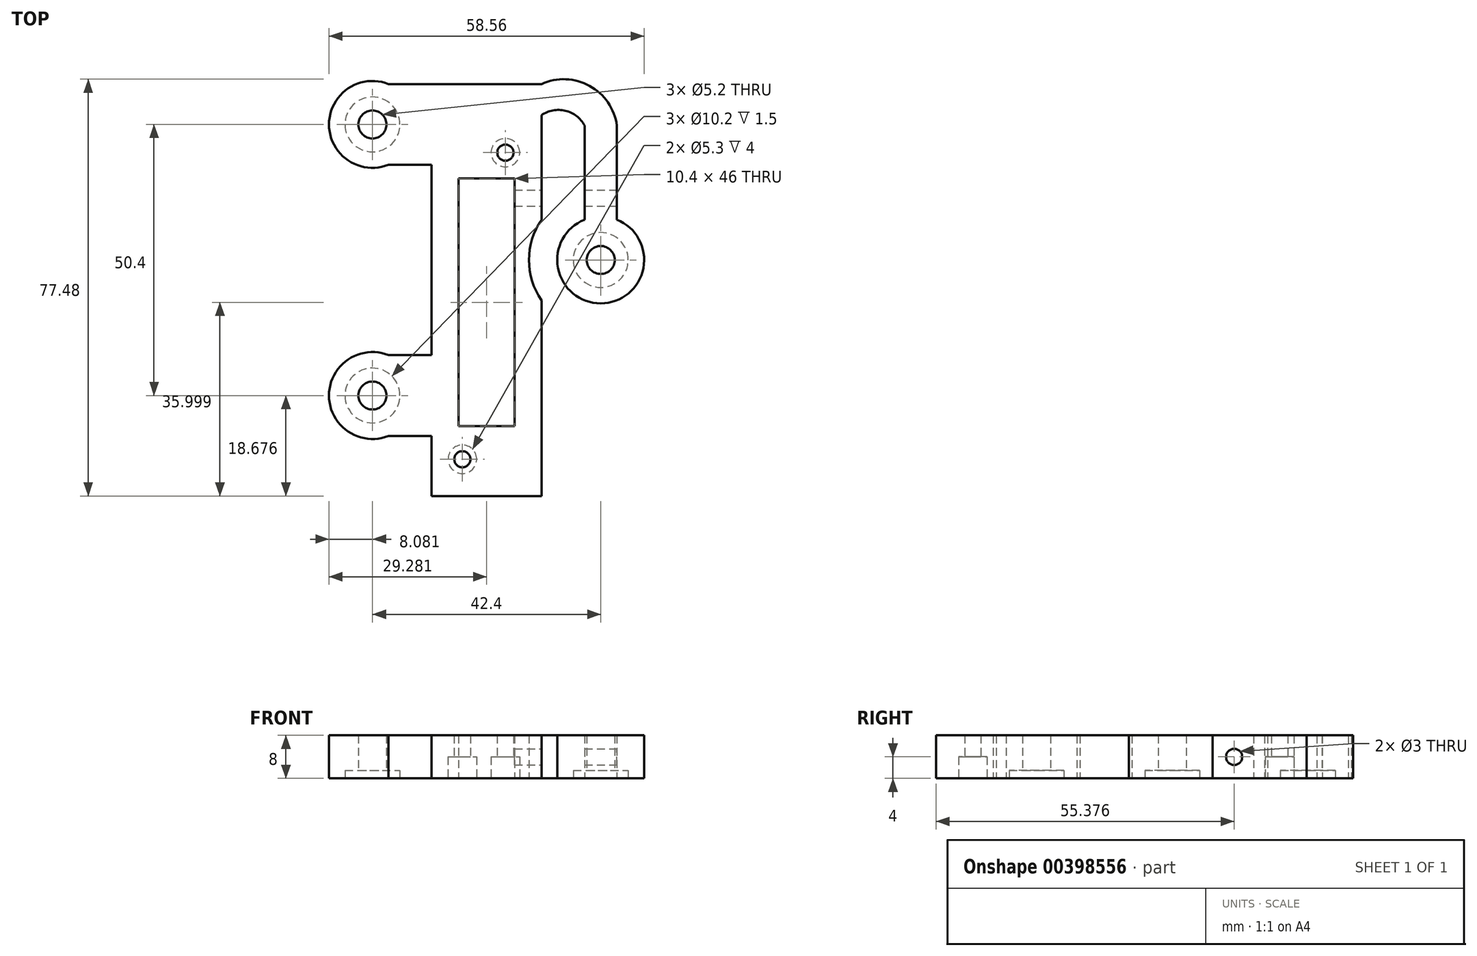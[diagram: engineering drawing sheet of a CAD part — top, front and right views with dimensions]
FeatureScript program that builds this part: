
annotation { "Feature Type Name" : "Feature", "Feature Type Description" : "" }
export const myFeature = defineFeature(function(context is Context, id is Id, definition is map)
    precondition{}
    {
        {
            var Q0;
            Q0=qCreatedBy(makeId("Top.planeOp"),FACE);
            var sketch = newSketch(context, id + "F0", { "sketchPlane" : qUnion([Q0])});
            skPoint(sketch, "E0", {"position": v(-7.75, -32.46) * mm});
            skPoint(sketch, "E1", {"position": v(0.25, 24.54) * mm});
            skCircle(sketch, "E2", {"center": v(0.25, 24.54) * mm, "radius": 1.5 * mm});
            skCircle(sketch, "E3", {"center": v(-7.75, -32.46) * mm, "radius": 1.5 * mm});
            skLineSegment(sketch, "E4.1", {"start": v(6.95, 37.29) * mm, "end": v(-13.45, 37.29) * mm});
            skLineSegment(sketch, "E4.2", {"start": v(6.95, -28.11) * mm, "end": v(6.95, 37.29) * mm});
            skLineSegment(sketch, "E4.3", {"start": v(-13.45, -28.11) * mm, "end": v(-13.45, 37.29) * mm});
            skLineSegment(sketch, "E5.bottom", {"start": v(-13.45, 37.29) * mm, "end": v(-21.45, 37.29) * mm});
            skLineSegment(sketch, "E5.top", {"start": v(-13.45, 22.29) * mm, "end": v(-21.45, 22.29) * mm});
            skLineSegment(sketch, "E5.left", {"start": v(-13.45, 37.29) * mm, "end": v(-13.45, 22.29) * mm});
            skLineSegment(sketch, "E5.right", {"start": v(-21.45, 37.29) * mm, "end": v(-21.45, 22.29) * mm});
            skLineSegment(sketch, "E6.bottom", {"start": v(-13.45, -28.11) * mm, "end": v(-21.45, -28.11) * mm});
            skLineSegment(sketch, "E6.top", {"start": v(-13.45, -13.11) * mm, "end": v(-21.45, -13.11) * mm});
            skLineSegment(sketch, "E6.left", {"start": v(-13.45, -28.11) * mm, "end": v(-13.45, -13.11) * mm});
            skLineSegment(sketch, "E6.right", {"start": v(-21.45, -28.11) * mm, "end": v(-21.45, -13.11) * mm});
            skLineSegment(sketch, "E7.left", {"start": v(6.95, 12.09) * mm, "end": v(6.95, -2.91) * mm});
            skLineSegment(sketch, "E7.right", {"start": v(14.95, 12.09) * mm, "end": v(14.95, -2.91) * mm});
            skPoint(sketch, "E8", {"position": v(17.95, 4.59) * mm});
            skPoint(sketch, "E8.positionSnap0", {"position": v(14.95, 4.59) * mm});
            skPoint(sketch, "E9", {"position": v(-24.45, -20.61) * mm});
            skPoint(sketch, "E9.positionSnap0", {"position": v(-21.45, -20.61) * mm});
            skPoint(sketch, "E10", {"position": v(-24.45, 29.79) * mm});
            skPoint(sketch, "E10.positionSnap0", {"position": v(-21.45, 29.79) * mm});
            skCircle(sketch, "E11", {"center": v(-24.45, 29.79) * mm, "radius": 8.08 * mm});
            skCircle(sketch, "E12", {"center": v(17.95, 4.59) * mm, "radius": 8.08 * mm});
            skCircle(sketch, "E13", {"center": v(-24.45, -20.61) * mm, "radius": 8.08 * mm});
            skArc(sketch, "E14", {"start": v(6.95, 12.09) * mm, "mid": v(4.64, 4.59) * mm, "end": v(6.95, -2.91) * mm});
            skLineSegment(sketch, "E15.bottom", {"start": v(14.95, 12.09) * mm, "end": v(20.95, 12.09) * mm});
            skLineSegment(sketch, "E15.left", {"start": v(14.95, 12.09) * mm, "end": v(14.95, 29.58) * mm});
            skLineSegment(sketch, "E15.right", {"start": v(20.95, 12.09) * mm, "end": v(20.95, 29.58) * mm});
            skPoint(sketch, "E16.third.point", {"position": v(11.8, 18.33) * mm});
            skArc(sketch, "E17", {"start": v(14.95, 29.58) * mm, "mid": v(11.38, 32.33) * mm, "end": v(6.95, 31.48) * mm});
            skPoint(sketch, "E17.second.point", {"position": v(6.95, 31.48) * mm});
            skPoint(sketch, "E17.third.point", {"position": v(4.8, 25.59) * mm});
            skArc(sketch, "E18.trimOffspring", {"start": v(20.95, 26.92) * mm, "mid": v(17.02, 36.24) * mm, "end": v(6.95, 37.29) * mm});
            skLineSegment(sketch, "E19.bottom", {"start": v(1.2, 19.7) * mm, "end": v(-1.2, 19.7) * mm});
            skPoint(sketch, "E20", {"position": v(6.95, 16.9) * mm});
            skPoint(sketch, "E20.positionSnap0", {"position": v(1.2, 16.9) * mm});
            skLineSegment(sketch, "E21", {"start": v(-13.45, -28.11) * mm, "end": v(-13.45, -39.3) * mm});
            skLineSegment(sketch, "E22", {"start": v(-13.45, -39.3) * mm, "end": v(6.95, -39.3) * mm});
            skLineSegment(sketch, "E23", {"start": v(6.95, -39.3) * mm, "end": v(6.95, -28.11) * mm});
            skPoint(sketch, "E4.0.start.orphan", {"position": v(6.95, -28.11) * mm});
            skLineSegment(sketch, "E24.bottom", {"start": v(1.95, -26.3) * mm, "end": v(-8.45, -26.3) * mm});
            skLineSegment(sketch, "E24.top", {"start": v(1.95, 19.7) * mm, "end": v(-8.45, 19.7) * mm});
            skLineSegment(sketch, "E24.left", {"start": v(1.95, -26.3) * mm, "end": v(1.95, 19.7) * mm});
            skLineSegment(sketch, "E24.right", {"start": v(-8.45, -26.3) * mm, "end": v(-8.45, 19.7) * mm});
            skSolve(sketch);
        }
        {
            var Q0;
            {var subQ0=sQuery(id+"F0.wireOp",EDGE,"E5.right");Q0=makeQuery(id+"F0.imprint","IMPRINT",FACE,{"disambiguationData":[TD([[makeQuery(id+"F0.imprint","IMPRINT",EDGE,{"derivedFrom":subQ0}),-1.0]])]});}
            var Q1;
            {var subQ0=sQuery(id+"F0.wireOp",EDGE,"E5.right");Q1=makeQuery(id+"F0.imprint","IMPRINT",FACE,{"disambiguationData":[TD([[makeQuery(id+"F0.imprint","IMPRINT",EDGE,{"derivedFrom":subQ0}),1.0]])]});}
            var Q2;
            {var subQ0=sQuery(id+"F0.wireOp",EDGE,"E5.bottom");Q2=makeQuery(id+"F0.imprint","IMPRINT",FACE,{"disambiguationData":[TD([[makeQuery(id+"F0.imprint","IMPRINT",EDGE,{"derivedFrom":subQ0}),1.0]])]});}
            var Q3;
            Q3=makeQuery(id+"F0.imprint","IMPRINT",FACE,{"disambiguationData":[TD([[makeQuery(id+"F0.imprint","IMPRINT",EDGE,{"derivedFrom":sQuery(id+"F0.wireOp",EDGE,"E2")}),-1.0]])]});
            var Q4;
            {var subQ9=sQuery(id+"F0.wireOp",EDGE,"E15.left");Q4=makeQuery(id+"F0.imprint","IMPRINT",FACE,{"disambiguationData":[TD([[makeQuery(id+"F0.imprint","IMPRINT",EDGE,{"derivedFrom":subQ9}),-1.0]])]});}
            var Q5;
            {var subQ0=sQuery(id+"F0.wireOp",EDGE,"E7.right");Q5=makeQuery(id+"F0.imprint","IMPRINT",FACE,{"disambiguationData":[TD([[makeQuery(id+"F0.imprint","IMPRINT",EDGE,{"derivedFrom":subQ0}),1.0]])]});}
            var Q6;
            {var subQ0=sQuery(id+"F0.wireOp",EDGE,"E15.bottom");Q6=makeQuery(id+"F0.imprint","IMPRINT",FACE,{"disambiguationData":[TD([[makeQuery(id+"F0.imprint","IMPRINT",EDGE,{"derivedFrom":subQ0}),1.0]])]});}
            var Q7;
            {var subQ0=sQuery(id+"F0.wireOp",EDGE,"E7.right");Q7=makeQuery(id+"F0.imprint","IMPRINT",FACE,{"disambiguationData":[TD([[makeQuery(id+"F0.imprint","IMPRINT",EDGE,{"derivedFrom":subQ0}),-1.0]])]});}
            var Q8;
            {var subQ0=sQuery(id+"F0.wireOp",EDGE,"E6.bottom");Q8=makeQuery(id+"F0.imprint","IMPRINT",FACE,{"disambiguationData":[TD([[makeQuery(id+"F0.imprint","IMPRINT",EDGE,{"derivedFrom":subQ0}),-1.0]])]});}
            var Q9;
            {var subQ0=sQuery(id+"F0.wireOp",EDGE,"E6.right");Q9=makeQuery(id+"F0.imprint","IMPRINT",FACE,{"disambiguationData":[TD([[makeQuery(id+"F0.imprint","IMPRINT",EDGE,{"derivedFrom":subQ0}),-1.0]])]});}
            var Q10;
            {var subQ0=sQuery(id+"F0.wireOp",EDGE,"E6.right");Q10=makeQuery(id+"F0.imprint","IMPRINT",FACE,{"disambiguationData":[TD([[makeQuery(id+"F0.imprint","IMPRINT",EDGE,{"derivedFrom":subQ0}),1.0]])]});}
            extrude(context, id + "F1", {"entities" : qUnion([Q0, Q1, Q2, Q3, Q4, Q5, Q6, Q7, Q8, Q9, Q10]), "depth" : 8 * mm, "offsetDistance" : 25 * mm});
        }
        {
            var Q0;
            Q0=sQuery(id+"F0.wireOp",VERTEX,"E8");
            var Q1;
            Q1=sQuery(id+"F0.wireOp",VERTEX,"E10");
            var Q2;
            Q2=sQuery(id+"F0.wireOp",VERTEX,"E9");
            var Q3;
            Q3=makeQuery(id+"F1.opExtrude","SWEPT_BODY",BODY,{"disambiguationData":[OSD([sQuery(id+"F0.wireOp",EDGE,"E2"),sQuery(id+"F0.wireOp",EDGE,"E3"),sQuery(id+"F0.wireOp",EDGE,"E4.0"),sQuery(id+"F0.wireOp",EDGE,"E4.1"),sQuery(id+"F0.wireOp",EDGE,"E4.2"),sQuery(id+"F0.wireOp",EDGE,"E4.3"),sQuery(id+"F0.wireOp",EDGE,"E5.bottom"),sQuery(id+"F0.wireOp",EDGE,"E5.top"),sQuery(id+"F0.wireOp",EDGE,"E6.bottom"),sQuery(id+"F0.wireOp",EDGE,"E6.top"),sQuery(id+"F0.wireOp",EDGE,"E11"),sQuery(id+"F0.wireOp",EDGE,"E12"),sQuery(id+"F0.wireOp",EDGE,"E13"),sQuery(id+"F0.wireOp",EDGE,"E14"),sQuery(id+"F0.wireOp",EDGE,"E15.left"),sQuery(id+"F0.wireOp",EDGE,"E15.right"),sQuery(id+"F0.wireOp",EDGE,"E17"),sQuery(id+"F0.wireOp",EDGE,"E18.trimOffspring"),sQuery(id+"F0.wireOp",EDGE,"E19.bottom"),sQuery(id+"F0.wireOp",EDGE,"E19.top"),sQuery(id+"F0.wireOp",EDGE,"E19.left"),sQuery(id+"F0.wireOp",EDGE,"E19.right")])]});
            hole(context, id + "F2", {"style" : HoleStyle.C_BORE, "endStyle" : HoleEndStyle.BLIND, "oppositeDirection" : true, "holeDiameter" : 5.2 * mm, "cBoreDiameter" : 10.2 * mm, "cBoreDepth" : 1.5 * mm, "majorDiameter" : 5 * mm, "holeDepth" : 30 * mm, "isTappedThrough" : true, "tappedDepth" : 12 * mm, "tapClearance" : 3, "locations" : qUnion([Q0, Q1, Q2]), "scope" : qUnion([Q3])});
        }
        {
            var Q0;
            Q0=makeQuery(id+"F1.opExtrude","SWEPT_FACE",FACE,{"disambiguationData":[OSD([sQuery(id+"F0.wireOp",EDGE,"E15.right")])]});
            var sketch = newSketch(context, id + "F3", { "sketchPlane" : qUnion([Q0])});
            skPoint(sketch, "E25", {"position": v(16.09, 4) * mm});
            skSolve(sketch);
        }
        {
            var Q0;
            Q0=sQuery(id+"F3.wireOp",VERTEX,"E25");
            var Q1;
            Q1=makeQuery(id+"F1.opExtrude","SWEPT_BODY",BODY,{"disambiguationData":[OSD([sQuery(id+"F0.wireOp",EDGE,"E2"),sQuery(id+"F0.wireOp",EDGE,"E3"),sQuery(id+"F0.wireOp",EDGE,"E4.1"),sQuery(id+"F0.wireOp",EDGE,"E4.2"),sQuery(id+"F0.wireOp",EDGE,"E4.3"),sQuery(id+"F0.wireOp",EDGE,"E5.bottom"),sQuery(id+"F0.wireOp",EDGE,"E5.top"),sQuery(id+"F0.wireOp",EDGE,"E6.bottom"),sQuery(id+"F0.wireOp",EDGE,"E6.top"),sQuery(id+"F0.wireOp",EDGE,"E11"),sQuery(id+"F0.wireOp",EDGE,"E12"),sQuery(id+"F0.wireOp",EDGE,"E13"),sQuery(id+"F0.wireOp",EDGE,"E14"),sQuery(id+"F0.wireOp",EDGE,"E15.left"),sQuery(id+"F0.wireOp",EDGE,"E15.right"),sQuery(id+"F0.wireOp",EDGE,"E17"),sQuery(id+"F0.wireOp",EDGE,"E18.trimOffspring"),sQuery(id+"F0.wireOp",EDGE,"E21"),sQuery(id+"F0.wireOp",EDGE,"E22"),sQuery(id+"F0.wireOp",EDGE,"E23"),sQuery(id+"F0.wireOp",EDGE,"E24.bottom"),sQuery(id+"F0.wireOp",EDGE,"E24.top"),sQuery(id+"F0.wireOp",EDGE,"E24.left"),sQuery(id+"F0.wireOp",EDGE,"E24.right")])]});
            hole(context, id + "F4", {"style" : HoleStyle.SIMPLE, "endStyle" : HoleEndStyle.BLIND, "holeDiameter" : 3 * mm, "majorDiameter" : 5 * mm, "holeDepth" : 20 * mm, "isTappedThrough" : true, "tappedDepth" : 12 * mm, "tapClearance" : 3, "locations" : qUnion([Q0]), "scope" : qUnion([Q1])});
        }
        {
            var Q0;
            Q0=sQuery(id+"F0.wireOp",VERTEX,"E1");
            var Q1;
            Q1=sQuery(id+"F0.wireOp",VERTEX,"E0");
            var Q2;
            Q2=makeQuery(id+"F1.opExtrude","SWEPT_BODY",BODY,{"disambiguationData":[OSD([sQuery(id+"F0.wireOp",EDGE,"E2"),sQuery(id+"F0.wireOp",EDGE,"E3"),sQuery(id+"F0.wireOp",EDGE,"E4.1"),sQuery(id+"F0.wireOp",EDGE,"E4.2"),sQuery(id+"F0.wireOp",EDGE,"E4.3"),sQuery(id+"F0.wireOp",EDGE,"E5.bottom"),sQuery(id+"F0.wireOp",EDGE,"E5.top"),sQuery(id+"F0.wireOp",EDGE,"E6.bottom"),sQuery(id+"F0.wireOp",EDGE,"E6.top"),sQuery(id+"F0.wireOp",EDGE,"E11"),sQuery(id+"F0.wireOp",EDGE,"E12"),sQuery(id+"F0.wireOp",EDGE,"E13"),sQuery(id+"F0.wireOp",EDGE,"E14"),sQuery(id+"F0.wireOp",EDGE,"E15.left"),sQuery(id+"F0.wireOp",EDGE,"E15.right"),sQuery(id+"F0.wireOp",EDGE,"E17"),sQuery(id+"F0.wireOp",EDGE,"E18.trimOffspring"),sQuery(id+"F0.wireOp",EDGE,"E21"),sQuery(id+"F0.wireOp",EDGE,"E22"),sQuery(id+"F0.wireOp",EDGE,"E23"),sQuery(id+"F0.wireOp",EDGE,"E24.bottom"),sQuery(id+"F0.wireOp",EDGE,"E24.top"),sQuery(id+"F0.wireOp",EDGE,"E24.left"),sQuery(id+"F0.wireOp",EDGE,"E24.right")])]});
            hole(context, id + "F5", {"style" : HoleStyle.C_BORE, "endStyle" : HoleEndStyle.BLIND, "oppositeDirection" : true, "holeDiameter" : 3 * mm, "cBoreDiameter" : 5.3 * mm, "cBoreDepth" : 4 * mm, "majorDiameter" : 5 * mm, "holeDepth" : 20 * mm, "isTappedThrough" : true, "tappedDepth" : 12 * mm, "tapClearance" : 3, "locations" : qUnion([Q0, Q1]), "scope" : qUnion([Q2])});
        }
    });
